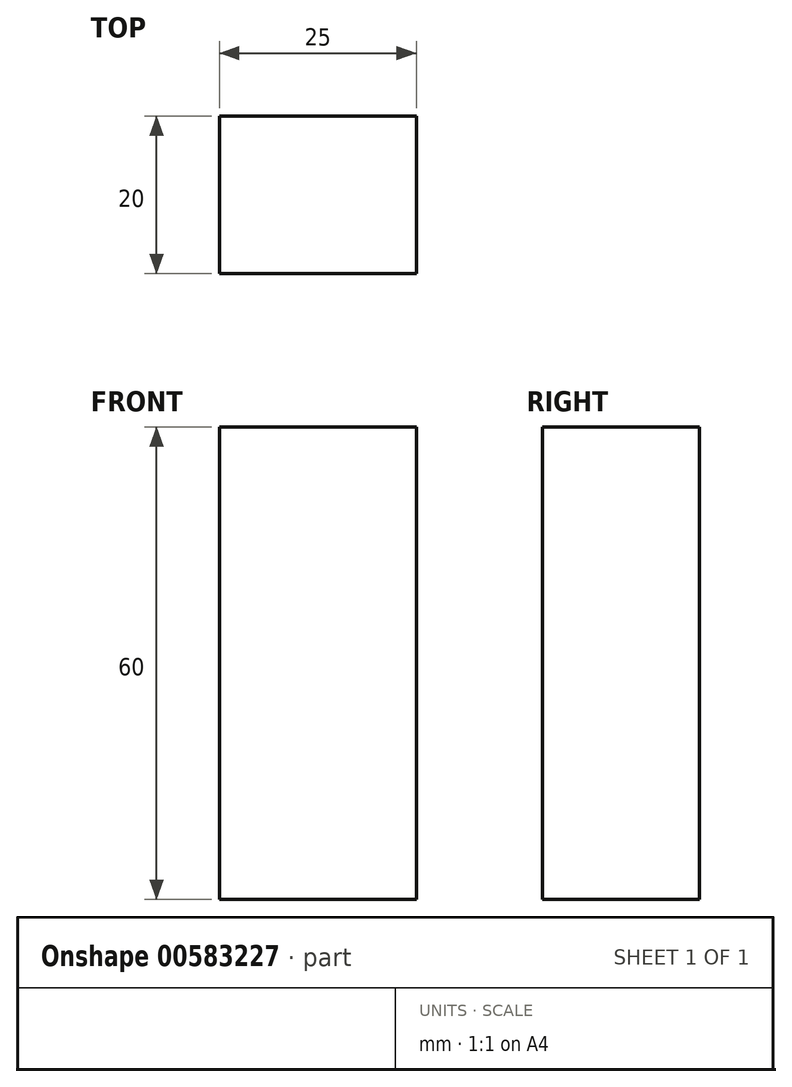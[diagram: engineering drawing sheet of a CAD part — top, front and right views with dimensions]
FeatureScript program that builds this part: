
annotation { "Feature Type Name" : "Feature", "Feature Type Description" : "" }
export const myFeature = defineFeature(function(context is Context, id is Id, definition is map)
    precondition{}
    {
        {
            var Q0;
            Q0=qCreatedBy(makeId("Front.planeOp"),FACE);
            var sketch = newSketch(context, id + "F0", { "sketchPlane" : qUnion([Q0])});
            skLineSegment(sketch, "E0.bottom", {"start": v(12.5, -30) * mm, "end": v(-12.5, -30) * mm});
            skLineSegment(sketch, "E0.top", {"start": v(12.5, 30) * mm, "end": v(-12.5, 30) * mm});
            skLineSegment(sketch, "E0.left", {"start": v(12.5, -30) * mm, "end": v(12.5, 30) * mm});
            skLineSegment(sketch, "E0.right", {"start": v(-12.5, -30) * mm, "end": v(-12.5, 30) * mm});
            skPoint(sketch, "E0.middle", {"position": v(0, 0) * mm});
            skSolve(sketch);
        }
        {
            var Q0;
            Q0=qSketchRegion(id+"F0",true);
            extrude(context, id + "F1", {"entities" : qUnion([Q0]), "endBound" : BoundingType.SYMMETRIC, "depth" : 20 * mm});
        }
    });
